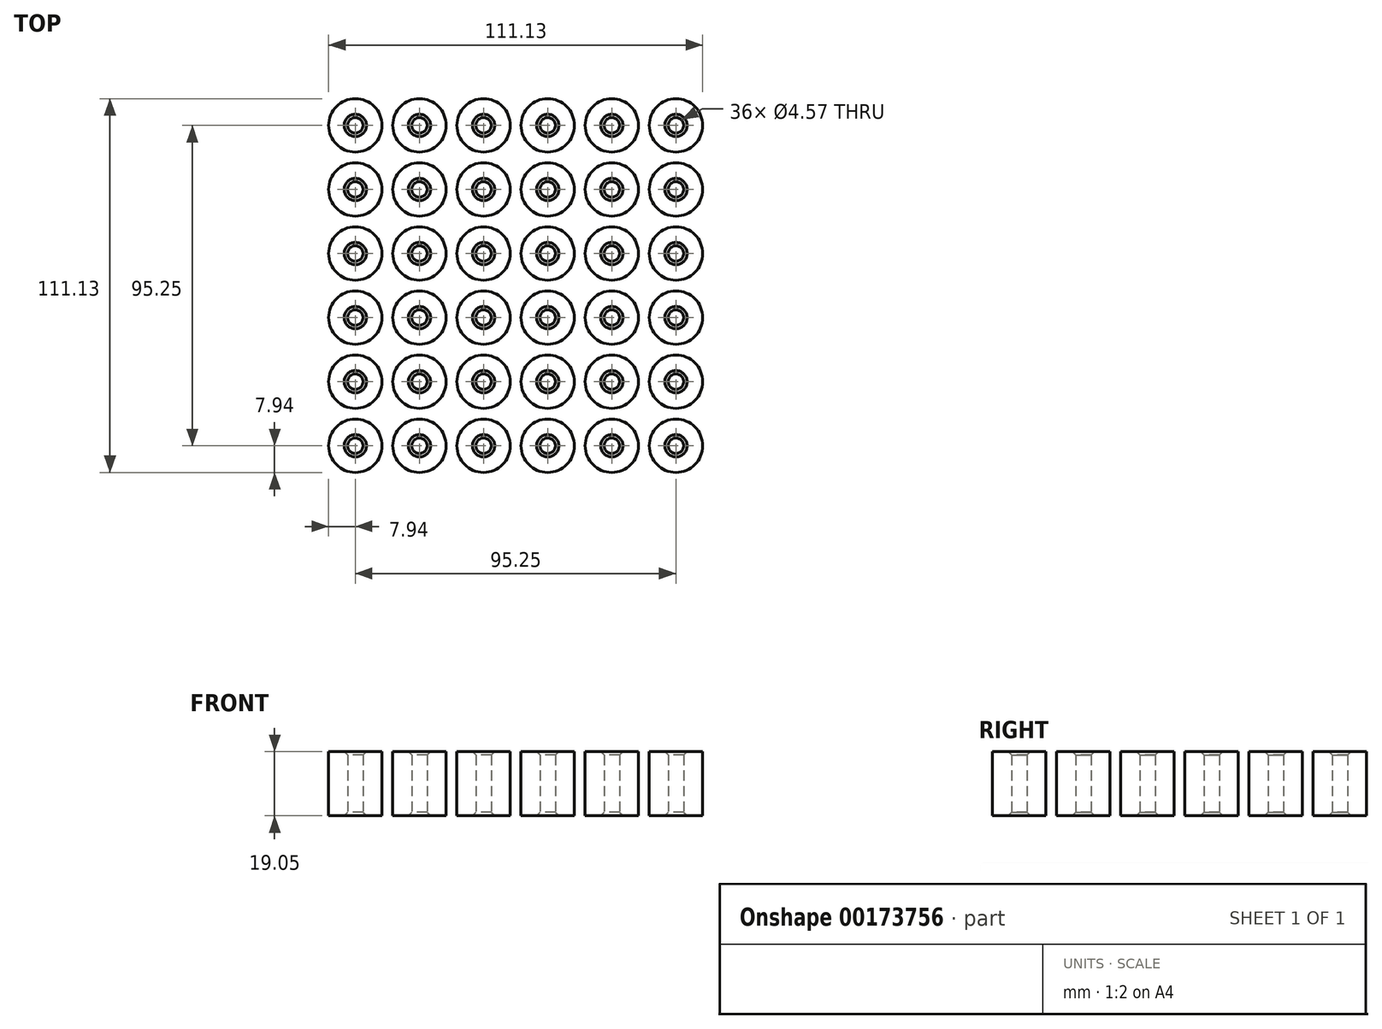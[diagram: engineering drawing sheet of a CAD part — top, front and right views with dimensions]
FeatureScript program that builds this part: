
annotation { "Feature Type Name" : "Feature", "Feature Type Description" : "" }
export const myFeature = defineFeature(function(context is Context, id is Id, definition is map)
    precondition{}
    {
        {
            var Q0;
            Q0=qCreatedBy(makeId("Top.planeOp"),FACE);
            var sketch = newSketch(context, id + "F0", { "sketchPlane" : qUnion([Q0])});
            skCircle(sketch, "E0", {"center": v(-63.5, -63.5) * mm, "radius": 7.94 * mm});
            skCircle(sketch, "E1", {"center": v(-63.5, -63.5) * mm, "radius": 2.29 * mm});
            skCircle(sketch, "E2.0.1.0", {"center": v(-63.5, -44.45) * mm, "radius": 7.94 * mm});
            skCircle(sketch, "E2.0.1.1", {"center": v(-63.5, -44.45) * mm, "radius": 2.29 * mm});
            skCircle(sketch, "E2.0.2.0", {"center": v(-63.5, -25.4) * mm, "radius": 7.94 * mm});
            skCircle(sketch, "E2.0.2.1", {"center": v(-63.5, -25.4) * mm, "radius": 2.29 * mm});
            skCircle(sketch, "E2.0.3.0", {"center": v(-63.5, -6.35) * mm, "radius": 7.94 * mm});
            skCircle(sketch, "E2.0.3.1", {"center": v(-63.5, -6.35) * mm, "radius": 2.29 * mm});
            skCircle(sketch, "E2.0.4.0", {"center": v(-63.5, 12.7) * mm, "radius": 7.94 * mm});
            skCircle(sketch, "E2.0.4.1", {"center": v(-63.5, 12.7) * mm, "radius": 2.29 * mm});
            skCircle(sketch, "E2.0.5.0", {"center": v(-63.5, 31.75) * mm, "radius": 7.94 * mm});
            skCircle(sketch, "E2.0.5.1", {"center": v(-63.5, 31.75) * mm, "radius": 2.29 * mm});
            skCircle(sketch, "E2.1.0.0", {"center": v(-44.45, -63.5) * mm, "radius": 7.94 * mm});
            skCircle(sketch, "E2.1.0.1", {"center": v(-44.45, -63.5) * mm, "radius": 2.29 * mm});
            skCircle(sketch, "E2.1.1.0", {"center": v(-44.45, -44.45) * mm, "radius": 7.94 * mm});
            skCircle(sketch, "E2.1.1.1", {"center": v(-44.45, -44.45) * mm, "radius": 2.29 * mm});
            skCircle(sketch, "E2.1.2.0", {"center": v(-44.45, -25.4) * mm, "radius": 7.94 * mm});
            skCircle(sketch, "E2.1.2.1", {"center": v(-44.45, -25.4) * mm, "radius": 2.29 * mm});
            skCircle(sketch, "E2.1.3.0", {"center": v(-44.45, -6.35) * mm, "radius": 7.94 * mm});
            skCircle(sketch, "E2.1.3.1", {"center": v(-44.45, -6.35) * mm, "radius": 2.29 * mm});
            skCircle(sketch, "E2.1.4.0", {"center": v(-44.45, 12.7) * mm, "radius": 7.94 * mm});
            skCircle(sketch, "E2.1.4.1", {"center": v(-44.45, 12.7) * mm, "radius": 2.29 * mm});
            skCircle(sketch, "E2.1.5.0", {"center": v(-44.45, 31.75) * mm, "radius": 7.94 * mm});
            skCircle(sketch, "E2.1.5.1", {"center": v(-44.45, 31.75) * mm, "radius": 2.29 * mm});
            skCircle(sketch, "E2.2.0.0", {"center": v(-25.4, -63.5) * mm, "radius": 7.94 * mm});
            skCircle(sketch, "E2.2.0.1", {"center": v(-25.4, -63.5) * mm, "radius": 2.29 * mm});
            skCircle(sketch, "E2.2.1.0", {"center": v(-25.4, -44.45) * mm, "radius": 7.94 * mm});
            skCircle(sketch, "E2.2.1.1", {"center": v(-25.4, -44.45) * mm, "radius": 2.29 * mm});
            skCircle(sketch, "E2.2.2.0", {"center": v(-25.4, -25.4) * mm, "radius": 7.94 * mm});
            skCircle(sketch, "E2.2.2.1", {"center": v(-25.4, -25.4) * mm, "radius": 2.29 * mm});
            skCircle(sketch, "E2.2.3.0", {"center": v(-25.4, -6.35) * mm, "radius": 7.94 * mm});
            skCircle(sketch, "E2.2.3.1", {"center": v(-25.4, -6.35) * mm, "radius": 2.29 * mm});
            skCircle(sketch, "E2.2.4.0", {"center": v(-25.4, 12.7) * mm, "radius": 7.94 * mm});
            skCircle(sketch, "E2.2.4.1", {"center": v(-25.4, 12.7) * mm, "radius": 2.29 * mm});
            skCircle(sketch, "E2.2.5.0", {"center": v(-25.4, 31.75) * mm, "radius": 7.94 * mm});
            skCircle(sketch, "E2.2.5.1", {"center": v(-25.4, 31.75) * mm, "radius": 2.29 * mm});
            skCircle(sketch, "E2.3.0.0", {"center": v(-6.35, -63.5) * mm, "radius": 7.94 * mm});
            skCircle(sketch, "E2.3.0.1", {"center": v(-6.35, -63.5) * mm, "radius": 2.29 * mm});
            skCircle(sketch, "E2.3.1.0", {"center": v(-6.35, -44.45) * mm, "radius": 7.94 * mm});
            skCircle(sketch, "E2.3.1.1", {"center": v(-6.35, -44.45) * mm, "radius": 2.29 * mm});
            skCircle(sketch, "E2.3.2.0", {"center": v(-6.35, -25.4) * mm, "radius": 7.94 * mm});
            skCircle(sketch, "E2.3.2.1", {"center": v(-6.35, -25.4) * mm, "radius": 2.29 * mm});
            skCircle(sketch, "E2.3.3.0", {"center": v(-6.35, -6.35) * mm, "radius": 7.94 * mm});
            skCircle(sketch, "E2.3.3.1", {"center": v(-6.35, -6.35) * mm, "radius": 2.29 * mm});
            skCircle(sketch, "E2.3.4.0", {"center": v(-6.35, 12.7) * mm, "radius": 7.94 * mm});
            skCircle(sketch, "E2.3.4.1", {"center": v(-6.35, 12.7) * mm, "radius": 2.29 * mm});
            skCircle(sketch, "E2.3.5.0", {"center": v(-6.35, 31.75) * mm, "radius": 7.94 * mm});
            skCircle(sketch, "E2.3.5.1", {"center": v(-6.35, 31.75) * mm, "radius": 2.29 * mm});
            skCircle(sketch, "E2.4.0.0", {"center": v(12.7, -63.5) * mm, "radius": 7.94 * mm});
            skCircle(sketch, "E2.4.0.1", {"center": v(12.7, -63.5) * mm, "radius": 2.29 * mm});
            skCircle(sketch, "E2.4.1.0", {"center": v(12.7, -44.45) * mm, "radius": 7.94 * mm});
            skCircle(sketch, "E2.4.1.1", {"center": v(12.7, -44.45) * mm, "radius": 2.29 * mm});
            skCircle(sketch, "E2.4.2.0", {"center": v(12.7, -25.4) * mm, "radius": 7.94 * mm});
            skCircle(sketch, "E2.4.2.1", {"center": v(12.7, -25.4) * mm, "radius": 2.29 * mm});
            skCircle(sketch, "E2.4.3.0", {"center": v(12.7, -6.35) * mm, "radius": 7.94 * mm});
            skCircle(sketch, "E2.4.3.1", {"center": v(12.7, -6.35) * mm, "radius": 2.29 * mm});
            skCircle(sketch, "E2.4.4.0", {"center": v(12.7, 12.7) * mm, "radius": 7.94 * mm});
            skCircle(sketch, "E2.4.4.1", {"center": v(12.7, 12.7) * mm, "radius": 2.29 * mm});
            skCircle(sketch, "E2.4.5.0", {"center": v(12.7, 31.75) * mm, "radius": 7.94 * mm});
            skCircle(sketch, "E2.4.5.1", {"center": v(12.7, 31.75) * mm, "radius": 2.29 * mm});
            skCircle(sketch, "E2.5.0.0", {"center": v(31.75, -63.5) * mm, "radius": 7.94 * mm});
            skCircle(sketch, "E2.5.0.1", {"center": v(31.75, -63.5) * mm, "radius": 2.29 * mm});
            skCircle(sketch, "E2.5.1.0", {"center": v(31.75, -44.45) * mm, "radius": 7.94 * mm});
            skCircle(sketch, "E2.5.1.1", {"center": v(31.75, -44.45) * mm, "radius": 2.29 * mm});
            skCircle(sketch, "E2.5.2.0", {"center": v(31.75, -25.4) * mm, "radius": 7.94 * mm});
            skCircle(sketch, "E2.5.2.1", {"center": v(31.75, -25.4) * mm, "radius": 2.29 * mm});
            skCircle(sketch, "E2.5.3.0", {"center": v(31.75, -6.35) * mm, "radius": 7.94 * mm});
            skCircle(sketch, "E2.5.3.1", {"center": v(31.75, -6.35) * mm, "radius": 2.29 * mm});
            skCircle(sketch, "E2.5.4.0", {"center": v(31.75, 12.7) * mm, "radius": 7.94 * mm});
            skCircle(sketch, "E2.5.4.1", {"center": v(31.75, 12.7) * mm, "radius": 2.29 * mm});
            skCircle(sketch, "E2.5.5.0", {"center": v(31.75, 31.75) * mm, "radius": 7.94 * mm});
            skCircle(sketch, "E2.5.5.1", {"center": v(31.75, 31.75) * mm, "radius": 2.29 * mm});
            skLineSegment(sketch, "E2.direction1", {"start": v(-63.5, -63.5) * mm, "end": v(-44.45, -63.5) * mm, "construction": true});
            skLineSegment(sketch, "E2.direction2", {"start": v(-63.5, -63.5) * mm, "end": v(-63.5, -44.45) * mm, "construction": true});
            skSolve(sketch);
        }
        {
            var Q0;
            Q0 = qSketchRegion(id + "F0", true);
            extrude(context, id + "F1", {"entities" : qUnion([Q0]), "depth" : 19.05 * mm});
        }
        {
            var Q0;
            Q0=makeQuery(id+"F1.opExtrude","CAP_EDGE",EDGE,{"disambiguationData":[OSD([sQuery(id+"F0.wireOp",EDGE,"E1")])],"isStart":false});
            var Q1;
            Q1=makeQuery(id+"F1.opExtrude","CAP_EDGE",EDGE,{"disambiguationData":[OSD([sQuery(id+"F0.wireOp",EDGE,"E2.1.0.1")])],"isStart":false});
            var Q2;
            Q2=makeQuery(id+"F1.opExtrude","CAP_EDGE",EDGE,{"disambiguationData":[OSD([sQuery(id+"F0.wireOp",EDGE,"E2.2.0.1")])],"isStart":false});
            var Q3;
            Q3=makeQuery(id+"F1.opExtrude","CAP_EDGE",EDGE,{"disambiguationData":[OSD([sQuery(id+"F0.wireOp",EDGE,"E2.3.0.1")])],"isStart":false});
            var Q4;
            Q4=makeQuery(id+"F1.opExtrude","CAP_EDGE",EDGE,{"disambiguationData":[OSD([sQuery(id+"F0.wireOp",EDGE,"E2.4.0.1")])],"isStart":false});
            var Q5;
            Q5=makeQuery(id+"F1.opExtrude","CAP_EDGE",EDGE,{"disambiguationData":[OSD([sQuery(id+"F0.wireOp",EDGE,"E2.5.0.1")])],"isStart":false});
            var Q6;
            Q6=makeQuery(id+"F1.opExtrude","CAP_EDGE",EDGE,{"disambiguationData":[OSD([sQuery(id+"F0.wireOp",EDGE,"E2.5.1.1")])],"isStart":false});
            var Q7;
            Q7=makeQuery(id+"F1.opExtrude","CAP_EDGE",EDGE,{"disambiguationData":[OSD([sQuery(id+"F0.wireOp",EDGE,"E2.4.1.1")])],"isStart":false});
            var Q8;
            Q8=makeQuery(id+"F1.opExtrude","CAP_EDGE",EDGE,{"disambiguationData":[OSD([sQuery(id+"F0.wireOp",EDGE,"E2.2.1.1")])],"isStart":false});
            var Q9;
            Q9=makeQuery(id+"F1.opExtrude","CAP_EDGE",EDGE,{"disambiguationData":[OSD([sQuery(id+"F0.wireOp",EDGE,"E2.3.1.1")])],"isStart":false});
            var Q10;
            Q10=makeQuery(id+"F1.opExtrude","CAP_EDGE",EDGE,{"disambiguationData":[OSD([sQuery(id+"F0.wireOp",EDGE,"E2.1.1.1")])],"isStart":false});
            var Q11;
            Q11=makeQuery(id+"F1.opExtrude","CAP_EDGE",EDGE,{"disambiguationData":[OSD([sQuery(id+"F0.wireOp",EDGE,"E2.0.1.1")])],"isStart":false});
            var Q12;
            Q12=makeQuery(id+"F1.opExtrude","CAP_EDGE",EDGE,{"disambiguationData":[OSD([sQuery(id+"F0.wireOp",EDGE,"E2.0.2.1")])],"isStart":false});
            var Q13;
            Q13=makeQuery(id+"F1.opExtrude","CAP_EDGE",EDGE,{"disambiguationData":[OSD([sQuery(id+"F0.wireOp",EDGE,"E2.1.2.1")])],"isStart":false});
            var Q14;
            Q14=makeQuery(id+"F1.opExtrude","CAP_EDGE",EDGE,{"disambiguationData":[OSD([sQuery(id+"F0.wireOp",EDGE,"E2.2.2.1")])],"isStart":false});
            var Q15;
            Q15=makeQuery(id+"F1.opExtrude","CAP_EDGE",EDGE,{"disambiguationData":[OSD([sQuery(id+"F0.wireOp",EDGE,"E2.3.2.1")])],"isStart":false});
            var Q16;
            Q16=makeQuery(id+"F1.opExtrude","CAP_EDGE",EDGE,{"disambiguationData":[OSD([sQuery(id+"F0.wireOp",EDGE,"E2.4.2.1")])],"isStart":false});
            var Q17;
            Q17=makeQuery(id+"F1.opExtrude","CAP_EDGE",EDGE,{"disambiguationData":[OSD([sQuery(id+"F0.wireOp",EDGE,"E2.5.2.1")])],"isStart":false});
            var Q18;
            Q18=makeQuery(id+"F1.opExtrude","CAP_EDGE",EDGE,{"disambiguationData":[OSD([sQuery(id+"F0.wireOp",EDGE,"E2.5.3.1")])],"isStart":false});
            var Q19;
            Q19=makeQuery(id+"F1.opExtrude","CAP_EDGE",EDGE,{"disambiguationData":[OSD([sQuery(id+"F0.wireOp",EDGE,"E2.0.3.1")])],"isStart":false});
            var Q20;
            Q20=makeQuery(id+"F1.opExtrude","CAP_EDGE",EDGE,{"disambiguationData":[OSD([sQuery(id+"F0.wireOp",EDGE,"E2.1.3.1")])],"isStart":false});
            var Q21;
            Q21=makeQuery(id+"F1.opExtrude","CAP_EDGE",EDGE,{"disambiguationData":[OSD([sQuery(id+"F0.wireOp",EDGE,"E2.2.3.1")])],"isStart":false});
            var Q22;
            Q22=makeQuery(id+"F1.opExtrude","CAP_EDGE",EDGE,{"disambiguationData":[OSD([sQuery(id+"F0.wireOp",EDGE,"E2.3.3.1")])],"isStart":false});
            var Q23;
            Q23=makeQuery(id+"F1.opExtrude","CAP_EDGE",EDGE,{"disambiguationData":[OSD([sQuery(id+"F0.wireOp",EDGE,"E2.4.3.1")])],"isStart":false});
            var Q24;
            Q24=makeQuery(id+"F1.opExtrude","CAP_EDGE",EDGE,{"disambiguationData":[OSD([sQuery(id+"F0.wireOp",EDGE,"E2.5.4.1")])],"isStart":false});
            var Q25;
            Q25=makeQuery(id+"F1.opExtrude","CAP_EDGE",EDGE,{"disambiguationData":[OSD([sQuery(id+"F0.wireOp",EDGE,"E2.4.4.1")])],"isStart":false});
            var Q26;
            Q26=makeQuery(id+"F1.opExtrude","CAP_EDGE",EDGE,{"disambiguationData":[OSD([sQuery(id+"F0.wireOp",EDGE,"E2.3.4.1")])],"isStart":false});
            var Q27;
            Q27=makeQuery(id+"F1.opExtrude","CAP_EDGE",EDGE,{"disambiguationData":[OSD([sQuery(id+"F0.wireOp",EDGE,"E2.2.4.1")])],"isStart":false});
            var Q28;
            Q28=makeQuery(id+"F1.opExtrude","CAP_EDGE",EDGE,{"disambiguationData":[OSD([sQuery(id+"F0.wireOp",EDGE,"E2.1.4.1")])],"isStart":false});
            var Q29;
            Q29=makeQuery(id+"F1.opExtrude","CAP_EDGE",EDGE,{"disambiguationData":[OSD([sQuery(id+"F0.wireOp",EDGE,"E2.0.4.1")])],"isStart":false});
            var Q30;
            Q30=makeQuery(id+"F1.opExtrude","CAP_EDGE",EDGE,{"disambiguationData":[OSD([sQuery(id+"F0.wireOp",EDGE,"E2.0.5.1")])],"isStart":false});
            var Q31;
            Q31=makeQuery(id+"F1.opExtrude","CAP_EDGE",EDGE,{"disambiguationData":[OSD([sQuery(id+"F0.wireOp",EDGE,"E2.1.5.1")])],"isStart":false});
            var Q32;
            Q32=makeQuery(id+"F1.opExtrude","CAP_EDGE",EDGE,{"disambiguationData":[OSD([sQuery(id+"F0.wireOp",EDGE,"E2.2.5.1")])],"isStart":false});
            var Q33;
            Q33=makeQuery(id+"F1.opExtrude","CAP_EDGE",EDGE,{"disambiguationData":[OSD([sQuery(id+"F0.wireOp",EDGE,"E2.3.5.1")])],"isStart":false});
            var Q34;
            Q34=makeQuery(id+"F1.opExtrude","CAP_EDGE",EDGE,{"disambiguationData":[OSD([sQuery(id+"F0.wireOp",EDGE,"E2.4.5.1")])],"isStart":false});
            var Q35;
            Q35=makeQuery(id+"F1.opExtrude","CAP_EDGE",EDGE,{"disambiguationData":[OSD([sQuery(id+"F0.wireOp",EDGE,"E2.5.5.1")])],"isStart":false});
            chamfer(context, id + "F2", {"entities" : qUnion([Q0, Q1, Q2, Q3, Q4, Q5, Q6, Q7, Q8, Q9, Q10, Q11, Q12, Q13, Q14, Q15, Q16, Q17, Q18, Q19, Q20, Q21, Q22, Q23, Q24, Q25, Q26, Q27, Q28, Q29, Q30, Q31, Q32, Q33, Q34, Q35]), "width" : 1.02 * mm, "tangentPropagation" : true});
        }
        {
            var Q0;
            Q0=makeQuery(id+"F1.opExtrude","CAP_EDGE",EDGE,{"disambiguationData":[OSD([sQuery(id+"F0.wireOp",EDGE,"E2.0.5.1")])],"isStart":true});
            var Q1;
            Q1=makeQuery(id+"F1.opExtrude","CAP_EDGE",EDGE,{"disambiguationData":[OSD([sQuery(id+"F0.wireOp",EDGE,"E2.0.4.1")])],"isStart":true});
            var Q2;
            Q2=makeQuery(id+"F1.opExtrude","CAP_EDGE",EDGE,{"disambiguationData":[OSD([sQuery(id+"F0.wireOp",EDGE,"E2.0.3.1")])],"isStart":true});
            var Q3;
            Q3=makeQuery(id+"F1.opExtrude","CAP_EDGE",EDGE,{"disambiguationData":[OSD([sQuery(id+"F0.wireOp",EDGE,"E2.0.2.1")])],"isStart":true});
            var Q4;
            Q4=makeQuery(id+"F1.opExtrude","CAP_EDGE",EDGE,{"disambiguationData":[OSD([sQuery(id+"F0.wireOp",EDGE,"E2.0.1.1")])],"isStart":true});
            var Q5;
            Q5=makeQuery(id+"F1.opExtrude","CAP_EDGE",EDGE,{"disambiguationData":[OSD([sQuery(id+"F0.wireOp",EDGE,"E1")])],"isStart":true});
            var Q6;
            Q6=makeQuery(id+"F1.opExtrude","CAP_EDGE",EDGE,{"disambiguationData":[OSD([sQuery(id+"F0.wireOp",EDGE,"E2.1.5.1")])],"isStart":true});
            var Q7;
            Q7=makeQuery(id+"F1.opExtrude","CAP_EDGE",EDGE,{"disambiguationData":[OSD([sQuery(id+"F0.wireOp",EDGE,"E2.1.4.1")])],"isStart":true});
            var Q8;
            Q8=makeQuery(id+"F1.opExtrude","CAP_EDGE",EDGE,{"disambiguationData":[OSD([sQuery(id+"F0.wireOp",EDGE,"E2.1.3.1")])],"isStart":true});
            var Q9;
            Q9=makeQuery(id+"F1.opExtrude","CAP_EDGE",EDGE,{"disambiguationData":[OSD([sQuery(id+"F0.wireOp",EDGE,"E2.1.2.1")])],"isStart":true});
            var Q10;
            Q10=makeQuery(id+"F1.opExtrude","CAP_EDGE",EDGE,{"disambiguationData":[OSD([sQuery(id+"F0.wireOp",EDGE,"E2.1.1.1")])],"isStart":true});
            var Q11;
            Q11=makeQuery(id+"F1.opExtrude","CAP_EDGE",EDGE,{"disambiguationData":[OSD([sQuery(id+"F0.wireOp",EDGE,"E2.1.0.1")])],"isStart":true});
            var Q12;
            Q12=makeQuery(id+"F1.opExtrude","CAP_EDGE",EDGE,{"disambiguationData":[OSD([sQuery(id+"F0.wireOp",EDGE,"E2.2.0.1")])],"isStart":true});
            var Q13;
            Q13=makeQuery(id+"F1.opExtrude","CAP_EDGE",EDGE,{"disambiguationData":[OSD([sQuery(id+"F0.wireOp",EDGE,"E2.2.1.1")])],"isStart":true});
            var Q14;
            Q14=makeQuery(id+"F1.opExtrude","CAP_EDGE",EDGE,{"disambiguationData":[OSD([sQuery(id+"F0.wireOp",EDGE,"E2.2.2.1")])],"isStart":true});
            var Q15;
            Q15=makeQuery(id+"F1.opExtrude","CAP_EDGE",EDGE,{"disambiguationData":[OSD([sQuery(id+"F0.wireOp",EDGE,"E2.2.3.1")])],"isStart":true});
            var Q16;
            Q16=makeQuery(id+"F1.opExtrude","CAP_EDGE",EDGE,{"disambiguationData":[OSD([sQuery(id+"F0.wireOp",EDGE,"E2.2.4.1")])],"isStart":true});
            var Q17;
            Q17=makeQuery(id+"F1.opExtrude","CAP_EDGE",EDGE,{"disambiguationData":[OSD([sQuery(id+"F0.wireOp",EDGE,"E2.2.5.1")])],"isStart":true});
            var Q18;
            Q18=makeQuery(id+"F1.opExtrude","CAP_EDGE",EDGE,{"disambiguationData":[OSD([sQuery(id+"F0.wireOp",EDGE,"E2.3.5.1")])],"isStart":true});
            var Q19;
            Q19=makeQuery(id+"F1.opExtrude","CAP_EDGE",EDGE,{"disambiguationData":[OSD([sQuery(id+"F0.wireOp",EDGE,"E2.3.4.1")])],"isStart":true});
            var Q20;
            Q20=makeQuery(id+"F1.opExtrude","CAP_EDGE",EDGE,{"disambiguationData":[OSD([sQuery(id+"F0.wireOp",EDGE,"E2.3.3.1")])],"isStart":true});
            var Q21;
            Q21=makeQuery(id+"F1.opExtrude","CAP_EDGE",EDGE,{"disambiguationData":[OSD([sQuery(id+"F0.wireOp",EDGE,"E2.3.2.1")])],"isStart":true});
            var Q22;
            Q22=makeQuery(id+"F1.opExtrude","CAP_EDGE",EDGE,{"disambiguationData":[OSD([sQuery(id+"F0.wireOp",EDGE,"E2.3.1.1")])],"isStart":true});
            var Q23;
            Q23=makeQuery(id+"F1.opExtrude","CAP_EDGE",EDGE,{"disambiguationData":[OSD([sQuery(id+"F0.wireOp",EDGE,"E2.4.5.1")])],"isStart":true});
            var Q24;
            Q24=makeQuery(id+"F1.opExtrude","CAP_EDGE",EDGE,{"disambiguationData":[OSD([sQuery(id+"F0.wireOp",EDGE,"E2.5.5.1")])],"isStart":true});
            var Q25;
            Q25=makeQuery(id+"F1.opExtrude","CAP_EDGE",EDGE,{"disambiguationData":[OSD([sQuery(id+"F0.wireOp",EDGE,"E2.5.4.1")])],"isStart":true});
            var Q26;
            Q26=makeQuery(id+"F1.opExtrude","CAP_EDGE",EDGE,{"disambiguationData":[OSD([sQuery(id+"F0.wireOp",EDGE,"E2.4.4.1")])],"isStart":true});
            var Q27;
            Q27=makeQuery(id+"F1.opExtrude","CAP_EDGE",EDGE,{"disambiguationData":[OSD([sQuery(id+"F0.wireOp",EDGE,"E2.4.3.1")])],"isStart":true});
            var Q28;
            Q28=makeQuery(id+"F1.opExtrude","CAP_EDGE",EDGE,{"disambiguationData":[OSD([sQuery(id+"F0.wireOp",EDGE,"E2.5.3.1")])],"isStart":true});
            var Q29;
            Q29=makeQuery(id+"F1.opExtrude","CAP_EDGE",EDGE,{"disambiguationData":[OSD([sQuery(id+"F0.wireOp",EDGE,"E2.5.2.1")])],"isStart":true});
            var Q30;
            Q30=makeQuery(id+"F1.opExtrude","CAP_EDGE",EDGE,{"disambiguationData":[OSD([sQuery(id+"F0.wireOp",EDGE,"E2.4.2.1")])],"isStart":true});
            var Q31;
            Q31=makeQuery(id+"F1.opExtrude","CAP_EDGE",EDGE,{"disambiguationData":[OSD([sQuery(id+"F0.wireOp",EDGE,"E2.4.1.1")])],"isStart":true});
            var Q32;
            Q32=makeQuery(id+"F1.opExtrude","CAP_EDGE",EDGE,{"disambiguationData":[OSD([sQuery(id+"F0.wireOp",EDGE,"E2.5.1.1")])],"isStart":true});
            var Q33;
            Q33=makeQuery(id+"F1.opExtrude","CAP_EDGE",EDGE,{"disambiguationData":[OSD([sQuery(id+"F0.wireOp",EDGE,"E2.4.0.1")])],"isStart":true});
            var Q34;
            Q34=makeQuery(id+"F1.opExtrude","CAP_EDGE",EDGE,{"disambiguationData":[OSD([sQuery(id+"F0.wireOp",EDGE,"E2.3.0.1")])],"isStart":true});
            var Q35;
            Q35=makeQuery(id+"F1.opExtrude","CAP_EDGE",EDGE,{"disambiguationData":[OSD([sQuery(id+"F0.wireOp",EDGE,"E2.5.0.1")])],"isStart":true});
            chamfer(context, id + "F3", {"entities" : qUnion([Q0, Q1, Q2, Q3, Q4, Q5, Q6, Q7, Q8, Q9, Q10, Q11, Q12, Q13, Q14, Q15, Q16, Q17, Q18, Q19, Q20, Q21, Q22, Q23, Q24, Q25, Q26, Q27, Q28, Q29, Q30, Q31, Q32, Q33, Q34, Q35]), "width" : 1.02 * mm, "tangentPropagation" : true});
        }
    });
